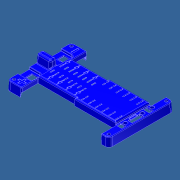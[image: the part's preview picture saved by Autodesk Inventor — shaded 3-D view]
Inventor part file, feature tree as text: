
AUTODESK INVENTOR PART (.ipt)
format: ipt  version: unknown  size: 5,939,200 bytes
history: native  units: mm (DEFAULTED — no unit token found)
features: extrude x32, sketch x27, fillet x20, other x10, pattern_linear x3, plane x3, projected_geometry x2, pattern_circular x1
ambient origin geometry x5: Origin, X Axis, Y Axis, Z Axis, Center Point
feature tree (98):
  other  "Main Body Sketch"
  other  "Primary Mounting Hole Axis"
  extrude  "Above the PCB Extrusion"  Depth=9.652mm
  extrude  "Below Extrusion"  Depth=217.0mm
  extrude  "Mounting Holes"  Depth=6.5278mm
  extrude  "Wago Holes"  Depth=209.55mm
  extrude  "Upper Level Boss"  Depth=142.875mm
  other  "Upper Level Bevel"
  other  "LED Sketch"
  extrude  "LED Holes"  Depth=2.54mm
  extrude  "LED Hole Up"  Depth=29.21mm
  extrude  "Lug Recesses"  Depth=2.54mm
  extrude  "Anti-Wrench Bump"  Depth=1.397mm
  fillet  "Pre Shell Fillet 1"  Radius=0.508mm
  extrude  "Mounting Hole Rib"  Depth=2.54mm
  other  "Mounting Hole Rib Draft"
  extrude  "Wago Hole Clearing"  Depth=15.0mm
  extrude  "Lug Holes"  Depth=10.0mm
  extrude  "Big CB Hole"  Depth=90.0mm
  extrude  "Big CB Holder Relief"  Depth=0.836185mm
  fillet  "Big CB Fillet 1"  Radius=2.159mm
  fillet  "Big CB Fillet 2"  Radius=1.7018mm
  pattern_linear  "Big CB Hole Pattern"  Count1=9  [1 undecoded]
  extrude  "Medium CB Holes"  Depth=0.508mm
  fillet  "Medium CB Fillet 1"  Radius=14.0mm
  fillet  "Medium CB Fillet 2"  Radius=1.6mm
  pattern_linear  "Medium CB Hole Pattern"  Count1=5  [1 undecoded]
  other  "Connector Holes"
  extrude  "Small Wago Holes"  Depth=2.54mm
  extrude  "cRio Connector Hole"  Depth=0.174533mm
  extrude  "cRio Connector Hole Clearance"  Depth=0.381mm
  extrude  "LED Hole Clearing"  Depth=13.762mm
  extrude  "Bottom Recess Cut"  Depth=29.1846mm
  extrude  "Side Cutouts for Bottom to Fill"  Depth=32.2834mm
  extrude  "Side Cutouts Extension"  Depth=0.254mm
  extrude  "Screw Bosses"  Depth=0.254mm
  other  "Ribs 1"
  extrude  "Main Rib"  Depth=0.254mm
  extrude  "Main Rib Component Cuts"  Depth=0.254mm
  extrude  "PS LED Rib"  Depth=15.0mm
  extrude  "Medium CB Holder Clearance Cuts"  Depth=70.0mm
  extrude  "Medium CB Area Ribs"  Depth=7.62mm
  other  "Bottom Support Ribs"
  extrude  "Battery Polarity Indicator Emboss"  Depth=7.62mm
  extrude  "LED FET Notch"  Depth=2.032mm TaperAngle=0.0deg
  other  "CB Indicator Sketch"
  extrude  "CB Indicator"  TaperAngle=0.0deg  [1 undecoded]
  fillet  "CB Indicator Fillet"  [1 undecoded]
  pattern_linear  "CB Indicator Pattern"  Spacing1=15.0deg  [1 undecoded]
  other  "CB Indicator Flip Axis"
  pattern_circular  "CB Indicator Flip"  [2 undecoded]
  fillet  "Through Hole Corner Fillets"  Radius=13.97mm
  fillet  "Top Fillets 1"  Radius=8.726646mm
  fillet  "Top Fillets 2"  Radius=0.349066mm
  fillet  "Top Fillets 3"  Radius=0.349066mm
  extrude  "Fillet Fill In / Undercut Prevention"  Depth=38.1mm
  fillet  "Bottom Fillets 1"  Radius=27.94mm
  fillet  "Bottom Intersection Fillets 1"  Radius=85.08mm
  fillet  "Mounting Hole, Bottom Recess Fillets"  Radius=5.207mm
  fillet  "Bottom Fillets 2"  Radius=34.7726mm
  fillet  "Rib Intersection Fillets"  Radius=2.032mm
  fillet  "Other Intersection Fillets"  Radius=2.032mm
  fillet  "Rib Edge Fillets"  Radius=0.523599mm
  fillet  "Through Hole Edge Fillets"  Radius=25.9842mm
  fillet  "Final Fillets 1"  Radius=99.70017mm
  fillet  "Final Fillets 2"  Radius=0.79375mm
  plane  "YZ Plane (RIGHT)"
  plane  "XZ Plane (TOP)"
  plane  "XY Plane (FRONT)"
  sketch  "Sketch7"  dims[d2=9.398mm d3=-0.523599mm d4=9.652mm d5=0.523599mm]
  sketch  "Sketch8"  dims[d6=2.54mm d12=217.0mm]
  sketch  "Sketch9"  dims[d13=135.1788mm d14=6.5278mm]
  sketch  "Sketch10"  dims[d15=127.0mm d16=209.55mm]
  sketch  "Sketch11"  dims[d19=225.425mm d20=142.875mm]
  sketch  "Sketch16"  dims[d21=7.9375mm d22=1.27mm d28=2.54mm d29=-0.349066mm]
  sketch  "Sketch17"  dims[d31=0.508mm d32=29.21mm]
  sketch  "Sketch21"  dims[d33=1.397mm d35=2.54mm d36=0.349066mm]
  sketch  "Sketch23"  dims[d37=80.0mm d39=10.0mm d41=1.397mm d42=0.508mm]
  sketch  "Sketch24"  dims[d43=13.843mm d44=2.54mm d45=0.349066mm]
  sketch  "Sketch25"  dims[d49=5.7023mm d50=15.0mm]
  sketch  "Sketch26"  dims[d51=60.0mm d53=15.0mm d54=10.0mm]
  sketch  "Sketch30"  dims[d55=81.7mm d56=90.0mm]
  sketch  "Sketch31"  dims[d57=28.8036mm d58=0.836185mm d61=2.159mm d64=1.7018mm]
  sketch  "Sketch32"  dims[d65=0.836185mm]
  sketch  "Sketch33"  dims[d68=1.7mm d71=90.0mm]
  sketch  "Sketch34"  dims[d72=2.059mm d73=0.508mm d74=14.0mm d76=1.6mm d77=50.0mm]
  sketch  "Sketch35"  dims[d78=1.0922mm d80=2.54mm d81=0.349066mm]
  sketch  "Sketch36"  dims[d84=2.54mm d85=0.349066mm d88=0.174533mm]
  projected_geometry  "Projected Loop2"
  projected_geometry  "Projected Loop3"
  sketch  "Sketch38"  dims[d90=90.0deg d91=0.381mm d92=-2.617994mm]
  sketch  "Sketch40"  dims[d93=13.762mm d94=13.762mm]
  sketch  "Sketch41"  dims[d95=32.2834mm d96=29.1846mm]
  sketch  "Sketch42"  dims[d98=21.0mm d102=32.2834mm]
  sketch  "Sketch43"  dims[d104=29.1846mm d110=0.254mm]
  sketch  "Sketch44"  dims[d112=0.254mm d113=0.254mm]
  sketch  "Sketch45"  dims[d114=25.4mm d115=-0.523599mm d116=0.254mm]
  sketch  "Sketch46"  dims[d117=0.254mm d118=0.254mm d119=15.0mm d121=70.0mm d122=7.62mm d123=7.62mm d124=2.032mm d125=1.524mm d127=0.0mm d128=0.0mm d129=15.0deg d130=15.0deg d131=1.524mm d132=13.97mm d135=8.726646mm d138=0.349066mm d139=0.349066mm d140=38.1mm d141=27.94mm d142=85.08mm d143=5.207mm d144=-0.349066mm d145=34.7726mm d147=2.032mm d148=2.032mm d155=0.523599mm d156=25.9842mm d157=99.70017mm d158=0.79375mm d159=0.508mm d160=9.398mm d161=8.509mm d163=4.9mm d164=7.62mm d165=0.349066mm d167=0.508mm d169=10.414mm d176=5.08mm d177=-2.617994mm d178=7.0mm d180=5.08mm d181=0.349066mm d182=15.0deg d183=5.08mm d184=4.0mm d185=1.869182mm d200=0.396875mm d201=0.396875mm d202=0.396875mm d203=0.396875mm d204=20.0mm d205=40.0mm d207=20.0mm d208=20.0mm d209=360.0deg d211=7.62mm d212=10.922mm d213=1.27mm d214=-0.349066mm d215=0.508mm d216=0.508mm d217=21.1mm d218=2.54mm d219=1.27mm d220=-0.349066mm d221=1.524mm d222=1.524mm d223=1.016mm d224=1.27mm d225=2.794mm d226=-0.349066mm d227=1.27mm d228=1.27mm d229=1.27mm d230=2.794mm d231=0.174533mm d232=3.6068mm d233=1.524mm d234=0.0mm d235=120.0mm d236=55.0mm d237=44.5mm d238=10.0mm d239=172.0mm d240=95.0mm d241=189.0mm d242=40.0mm d252=1.524mm d253=7.62mm d254=15.24mm d255=19.05mm d256=-0.523599mm d257=0.728441mm d258=3.81mm d262=0.396875mm d263=0.396875mm d264=0.396875mm d265=20.0mm d266=0.396875mm d267=0.396875mm d268=0.396875mm d269=0.79375mm d270=0.396875mm d277=1.397mm d278=2.54mm d279=0.174533mm d280=1.397mm d281=25.4mm d282=0.174533mm d284=0.523599mm d285=25.4mm d286=0.0mm d287=78.128mm d288=0.523599mm d289=5.588mm d293=110.236mm d294=91.2876mm d295=4.064mm d296=0.79375mm d298=0.254mm d299=0.396875mm d300=6.6548mm d302=1.524mm d303=13.962634mm d304=1.016mm d305=0.396875mm d306=0.79375mm d315=2.794mm d317=0.79375mm d318=0.508mm d319=2.794mm d320=1.27mm d321=0.79375mm d322=1.27mm d325=0.396875mm d326=7.239mm d328=7.8232mm d329=-0.349066mm d331=1.524mm d332=15.0mm d333=70.0mm d334=12.7mm d337=4.572mm d338=-0.523599mm d339=0.79375mm d340=25.4mm d341=1.22173mm d343=0.127mm d344=1.778mm d346=25.4mm d347=6.35mm d348=19.05mm d349=80.264mm d350=165.631mm d351=3.81mm d352=15.24mm d353=58.42mm d354=3.81mm d355=15.24mm d356=58.42mm d357=92.075mm d358=0.396875mm d360=0.396875mm d361=0.381mm d362=-2.617994mm d363=0.396875mm d364=0.127mm d365=1.27mm d366=1.27mm d367=1.27mm d368=1.27mm d372=0.635mm d373=25.4mm d374=-0.349066mm d375=0.635mm d377=0.635mm d378=0.635mm d379=0.254mm d380=0.127mm d382=33.5mm d383=6.35mm d384=0.508mm d385=1.778mm d386=0.508mm d387=0.6096mm d388=7.239mm d389=24.3078mm d390=0.5mm d391=0.25mm d393=13.4mm d395=8.5mm d396=0.508mm d397=15.0114mm d399=1.0668mm d400=-0.349066mm d401=1.0668mm d402=-0.349066mm d403=3.81mm d404=0.508mm d406=1.0668mm d407=0.523599mm d409=1.905mm d410=8.509mm d411=13.3096mm d412=14.0mm d413=35.7mm d414=23.5mm d415=7.0mm d416=7.0mm d417=26.1mm d418=3.5mm d419=0.088699mm d420=0.088699mm d421=4.363323mm d422=0.508mm d423=3.0mm d424=1.4mm d425=0.381mm d426=0.381mm d428=35.9305mm d429=32.0mm d430=1.27mm d431=-0.349066mm d434=0.396875mm d435=135.651mm d436=151.131mm d437=1.524mm d438=1.524mm d439=1.016mm d440=0.174533mm d441=1.592078mm d442=1.592078mm d443=1.592078mm d444=1.016mm d445=0.174533mm d446=1.778mm d447=1.592078mm d450=2.286mm d451=0.396875mm d452=2.286mm d453=1.016mm d454=0.396875mm d455=0.79375mm d456=0.396875mm d457=0.396875mm d458=0.396875mm d459=1.524mm d460=45.0deg d461=1.524mm d462=45.0deg d463=45.0deg d464=2.032mm d465=2.54mm d466=0.174533mm d467=0.254mm d472=25.4mm d473=0.349066mm d474=0.127mm d475=0.254mm d476=0.127mm d477=0.396875mm d478=0.254mm d479=0.79375mm d480=0.127mm d481=0.79375mm d484=7.62mm d485=0.632986mm d486=0.836185mm]
note: 7 required parameter values undecoded (feature->parameter linkage not recoverable at this tier; creation-order binding heuristic only, values carry confidence <= 0.55)
